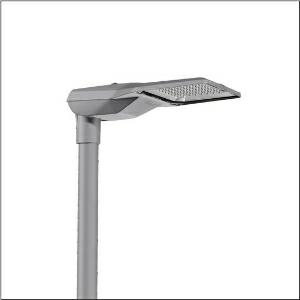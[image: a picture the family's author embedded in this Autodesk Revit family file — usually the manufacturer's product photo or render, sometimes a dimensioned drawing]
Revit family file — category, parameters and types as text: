
# Revit family: streetlight_sl_21_midi___p0_8ab_5xe3r33s08lb_9dc6
name_source: partatom
category: Lighting Fixtures
units: mm (PartAtom-declared; Revit-internal decimal feet)

## family parameters
Cut with Voids When Loaded = No
Host = Face
Light Source = No
Part Type = Normal
Room Calculation Point = No
Round Connector Dimension = Use Diameter
Shared = No

## types (1)
- --- (1 x LED, 12450 lm, 99.6 W, 3000K)
    Apparent Load = 100 VA
    CIE Flux Codes = 36 71 98 100 100
    Color Rendering = 70
    Color Temperature = 3000K
    Default Elevation = 1800 mm
    Description = Streetlight SL 21 midi, mast luminaire, primary light control with lens, of PMMA, primary optical cover: cover, of toughened safety glass, transparent, light distribution: P0.8aB, light emission: direct distribution, primary light characteristic: asymmetric, installation type: post-top, side-entry, LED, High Power LED, rated luminous flux: 12.450lm, luminous efficacy: 125lm/W, light colour: 730, colour temperature: 3000K, control gear: D4i, control: pre-setting: logarithmic dimming characteristic, flexible luminous flux parameterisation, time-dependent luminous flux control, constant luminous flux control, overheat protection, mains connection: 230..240V, AC, 50/60Hz, start of lifetime: 100W, end of service life: 102W, reduction: 46W, luminaire housing, of diecast aluminium, powder-coated, SITECO metallic grey (DB 702S), corrosivity category C5 high according to DIN EN ISO 12944, multi-level sealing system, sealing non-destructively replaceable, inclination adjustable: 0°, 5°, 10°, 15°, please order mast flange separately, length: 644mm, width: 335mm, height: 110mm, mast flange for spigot size: 42mm (side-entry): 5XC10008XM4, 60/48mm (side-entry/post-top): 5XC10108XM2, 76/60mm (side-entry/post-top): 5XC10108XM1, mounting height: 4..8m, Smart Interface above, protection rating (complete): IP66, insulation class (complete): insulation class II (safety insulation), certification: CE, ENEC, ENEC+, VDE, impact resistance: IK10, permissible operating ambient temperature for outdoor applications: -40..+50°C, standard-compliant lighting for roads and squares, packaging unit: 1 piece

Light Distribution: P0.8aB
    Height = 111 mm
    Lamp = 1 x LED
    Lamp Light Flux = 12450 lm
    Lamp Power = 99.6 W
    Lamp count = 1
    Length = 644 mm
    Luminous efficacy = 125 lm/W
    Manufacturer = Siteco
    ModVariant = No
    Model = 5XE3R33S08LB
    Number of Poles = 1
    OnlyDefault = Yes
    Power Factor = 1
    Product Name = Streetlight SL 21 midi | P0.8aB
    Product group = mast luminaire | pylon top
    ProductGroupID = 6100
    Protection Class = Protection class II
    Protection Degree = IP 66
    RLX_Detail_Level = 1
    RLX_Emergency_Light_Flux = 0 lm
    RLX_Emergency_Type = 0
    RLX_Emergency_Type_DB = No
    RlxData = <blob elided: 26501 chars, md5=890023ce>
    Socket = socket
    Standby Power = 0 W
    System Light Flux = 12450 lm
    System Power = 100 W
    Type Comments = factory setting: luminous flux: 100 % | dim-lin: 254 | 1020 mA
    Type Image = l_1004302.jpg
    URL = http://relux.com
    VarID = @adj_033305
    Voltage = 0 V
    Weight = 0.00 kg
    Width = 336 mm

## geometry (parser evidence)
native form markers: Blend x4, Sweep x13
no freeform markers — native parametric forms only
